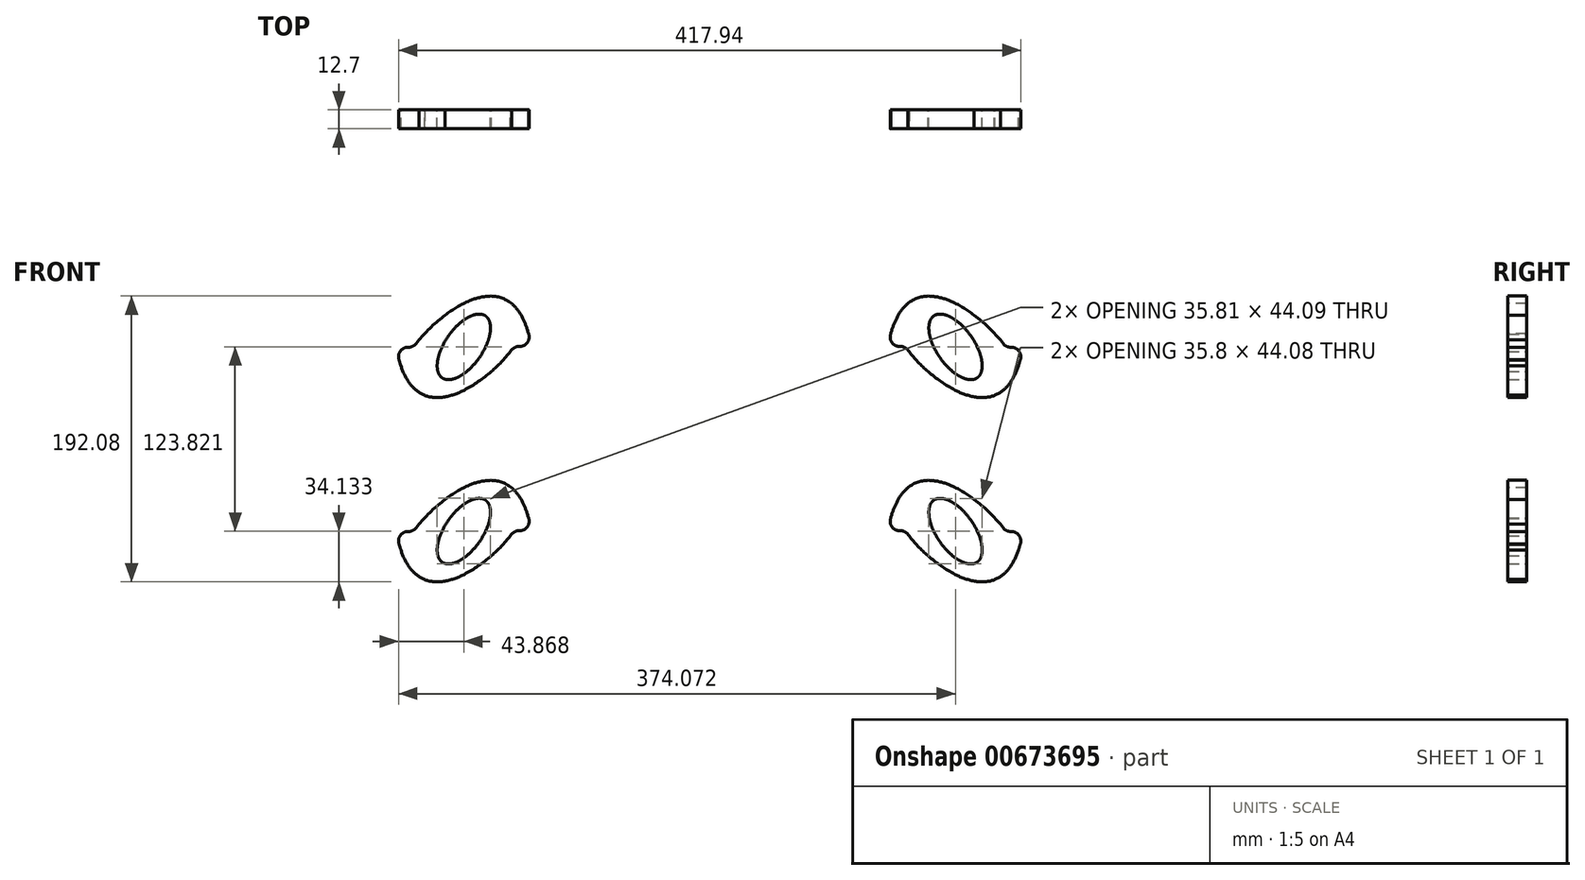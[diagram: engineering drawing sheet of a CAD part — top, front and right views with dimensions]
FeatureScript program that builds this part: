
annotation { "Feature Type Name" : "Feature", "Feature Type Description" : "" }
export const myFeature = defineFeature(function(context is Context, id is Id, definition is map)
    precondition{}
    {
        {
            var Q0;
            Q0=qCreatedBy(makeId("Front.planeOp"),FACE);
            var sketch = newSketch(context, id + "F0", { "sketchPlane" : qUnion([Q0])});
            skArc(sketch, "E0", {"start": v(-195.2, 79.62) * mm, "mid": v(-186.95, 88.48) * mm, "end": v(-177.7, 96.3) * mm});
            skArc(sketch, "E1", {"start": v(-177.7, 96.3) * mm, "mid": v(-169.74, 101.66) * mm, "end": v(-161.19, 106) * mm});
            skArc(sketch, "E2", {"start": v(-161.19, 106) * mm, "mid": v(-154.68, 108.16) * mm, "end": v(-147.88, 109.11) * mm});
            skArc(sketch, "E3", {"start": v(-147.88, 109.11) * mm, "mid": v(-140.03, 108.03) * mm, "end": v(-133.1, 104.19) * mm});
            skArc(sketch, "E4", {"start": v(-133.1, 104.19) * mm, "mid": v(-128.88, 99.71) * mm, "end": v(-125.64, 94.47) * mm});
            skArc(sketch, "E5", {"start": v(-125.64, 94.47) * mm, "mid": v(-123.38, 89.28) * mm, "end": v(-121.63, 83.89) * mm});
            skLineSegment(sketch, "E6", {"start": v(-121.63, 83.89) * mm, "end": v(-121.54, 83.6) * mm});
            skArc(sketch, "E7", {"start": v(-121.54, 83.6) * mm, "mid": v(-122.53, 77.79) * mm, "end": v(-127.86, 75.29) * mm});
            skArc(sketch, "E8", {"start": v(-127.86, 75.29) * mm, "mid": v(-130.86, 74.68) * mm, "end": v(-133.23, 72.74) * mm});
            skLineSegment(sketch, "E9", {"start": v(-133.23, 72.74) * mm, "end": v(-133.9, 71.83) * mm});
            skArc(sketch, "E10", {"start": v(-133.9, 71.83) * mm, "mid": v(-139.92, 64.83) * mm, "end": v(-146.63, 58.5) * mm});
            skArc(sketch, "E11", {"start": v(-146.63, 58.5) * mm, "mid": v(-155.36, 51.67) * mm, "end": v(-164.85, 45.94) * mm});
            skArc(sketch, "E12", {"start": v(-164.85, 45.94) * mm, "mid": v(-171.62, 43.03) * mm, "end": v(-178.77, 41.23) * mm});
            skArc(sketch, "E13", {"start": v(-178.77, 41.23) * mm, "mid": v(-185.1, 40.98) * mm, "end": v(-191.28, 42.4) * mm});
            skLineSegment(sketch, "E14", {"start": v(-191.28, 42.4) * mm, "end": v(-191.47, 42.47) * mm});
            skArc(sketch, "E15", {"start": v(-191.47, 42.47) * mm, "mid": v(-196.89, 45.66) * mm, "end": v(-201.23, 50.2) * mm});
            skArc(sketch, "E16", {"start": v(-201.23, 50.2) * mm, "mid": v(-204.77, 55.97) * mm, "end": v(-207.35, 62.21) * mm});
            skArc(sketch, "E17", {"start": v(-207.35, 62.21) * mm, "mid": v(-207.97, 64.12) * mm, "end": v(-208.54, 66.04) * mm});
            skLineSegment(sketch, "E18", {"start": v(-208.54, 66.04) * mm, "end": v(-208.64, 66.36) * mm});
            skArc(sketch, "E19", {"start": v(-208.64, 66.36) * mm, "mid": v(-207.71, 72.2) * mm, "end": v(-202.4, 74.74) * mm});
            skArc(sketch, "E20", {"start": v(-202.4, 74.74) * mm, "mid": v(-199.51, 75.32) * mm, "end": v(-197.2, 77.12) * mm});
            skLineSegment(sketch, "E21", {"start": v(-197.2, 77.12) * mm, "end": v(-195.2, 79.62) * mm});
            skArc(sketch, "E22", {"start": v(-179.67, 54.2) * mm, "mid": v(-178.37, 53.5) * mm, "end": v(-176.95, 53.1) * mm});
            skArc(sketch, "E23", {"start": v(-176.95, 53.1) * mm, "mid": v(-175.54, 52.97) * mm, "end": v(-174.13, 53.05) * mm});
            skArc(sketch, "E24", {"start": v(-174.13, 53.05) * mm, "mid": v(-172.49, 53.36) * mm, "end": v(-170.89, 53.86) * mm});
            skArc(sketch, "E25", {"start": v(-170.89, 53.86) * mm, "mid": v(-168.9, 54.7) * mm, "end": v(-167, 55.74) * mm});
            skArc(sketch, "E26", {"start": v(-167, 55.74) * mm, "mid": v(-164.64, 57.33) * mm, "end": v(-162.41, 59.1) * mm});
            skArc(sketch, "E27", {"start": v(-162.41, 59.1) * mm, "mid": v(-159.55, 61.82) * mm, "end": v(-156.93, 64.78) * mm});
            skArc(sketch, "E28", {"start": v(-156.93, 64.78) * mm, "mid": v(-155.79, 66.23) * mm, "end": v(-154.7, 67.73) * mm});
            skArc(sketch, "E29", {"start": v(-154.7, 67.73) * mm, "mid": v(-152.2, 71.67) * mm, "end": v(-150.1, 75.83) * mm});
            skArc(sketch, "E30", {"start": v(-150.1, 75.83) * mm, "mid": v(-148.93, 78.75) * mm, "end": v(-148.01, 81.76) * mm});
            skArc(sketch, "E31", {"start": v(-148.01, 81.76) * mm, "mid": v(-147.52, 84.07) * mm, "end": v(-147.24, 86.4) * mm});
            skArc(sketch, "E32", {"start": v(-147.24, 86.4) * mm, "mid": v(-147.2, 88.21) * mm, "end": v(-147.36, 90.02) * mm});
            skArc(sketch, "E33", {"start": v(-147.36, 90.02) * mm, "mid": v(-147.66, 91.45) * mm, "end": v(-148.15, 92.83) * mm});
            skArc(sketch, "E34", {"start": v(-148.15, 92.83) * mm, "mid": v(-148.8, 94.03) * mm, "end": v(-149.67, 95.1) * mm});
            skArc(sketch, "E35", {"start": v(-149.67, 95.1) * mm, "mid": v(-150.08, 95.47) * mm, "end": v(-150.53, 95.82) * mm});
            skArc(sketch, "E36", {"start": v(-150.53, 95.82) * mm, "mid": v(-151.83, 96.52) * mm, "end": v(-153.26, 96.93) * mm});
            skArc(sketch, "E37", {"start": v(-153.26, 96.93) * mm, "mid": v(-154.66, 97.06) * mm, "end": v(-156.07, 96.98) * mm});
            skArc(sketch, "E38", {"start": v(-156.07, 96.98) * mm, "mid": v(-157.72, 96.67) * mm, "end": v(-159.31, 96.17) * mm});
            skArc(sketch, "E39", {"start": v(-159.31, 96.17) * mm, "mid": v(-161.3, 95.32) * mm, "end": v(-163.2, 94.28) * mm});
            skArc(sketch, "E40", {"start": v(-163.2, 94.28) * mm, "mid": v(-165.56, 92.7) * mm, "end": v(-167.8, 90.92) * mm});
            skArc(sketch, "E41", {"start": v(-167.8, 90.92) * mm, "mid": v(-170.66, 88.2) * mm, "end": v(-173.28, 85.25) * mm});
            skArc(sketch, "E42", {"start": v(-173.28, 85.25) * mm, "mid": v(-174.42, 83.8) * mm, "end": v(-175.5, 82.3) * mm});
            skArc(sketch, "E43", {"start": v(-175.5, 82.3) * mm, "mid": v(-178, 78.36) * mm, "end": v(-180.1, 74.2) * mm});
            skArc(sketch, "E44", {"start": v(-180.1, 74.2) * mm, "mid": v(-181.27, 71.27) * mm, "end": v(-182.19, 68.26) * mm});
            skArc(sketch, "E45", {"start": v(-182.19, 68.26) * mm, "mid": v(-182.68, 65.96) * mm, "end": v(-182.96, 63.62) * mm});
            skArc(sketch, "E46", {"start": v(-182.96, 63.62) * mm, "mid": v(-183, 61.81) * mm, "end": v(-182.84, 60) * mm});
            skArc(sketch, "E47", {"start": v(-182.84, 60) * mm, "mid": v(-182.54, 58.58) * mm, "end": v(-182.05, 57.2) * mm});
            skArc(sketch, "E48", {"start": v(-182.05, 57.2) * mm, "mid": v(-181.4, 56) * mm, "end": v(-180.54, 54.94) * mm});
            skArc(sketch, "E49", {"start": v(-180.54, 54.94) * mm, "mid": v(-180.12, 54.55) * mm, "end": v(-179.67, 54.2) * mm});
            skLineSegment(sketch, "E50", {"start": v(195.2, -44.2) * mm, "end": v(197.2, -46.7) * mm});
            skArc(sketch, "E51", {"start": v(197.2, -46.7) * mm, "mid": v(199.51, -48.5) * mm, "end": v(202.4, -49.08) * mm});
            skArc(sketch, "E52", {"start": v(202.4, -49.08) * mm, "mid": v(207.71, -51.63) * mm, "end": v(208.64, -57.46) * mm});
            skLineSegment(sketch, "E53", {"start": v(208.64, -57.46) * mm, "end": v(208.54, -57.78) * mm});
            skArc(sketch, "E54", {"start": v(208.54, -57.78) * mm, "mid": v(207.97, -59.7) * mm, "end": v(207.35, -61.6) * mm});
            skArc(sketch, "E55", {"start": v(207.35, -61.6) * mm, "mid": v(204.77, -67.85) * mm, "end": v(201.23, -73.62) * mm});
            skArc(sketch, "E56", {"start": v(201.23, -73.62) * mm, "mid": v(196.89, -78.16) * mm, "end": v(191.47, -81.35) * mm});
            skLineSegment(sketch, "E57", {"start": v(191.47, -81.35) * mm, "end": v(191.28, -81.43) * mm});
            skArc(sketch, "E58", {"start": v(191.28, -81.43) * mm, "mid": v(185.1, -82.84) * mm, "end": v(178.77, -82.6) * mm});
            skArc(sketch, "E59", {"start": v(178.77, -82.6) * mm, "mid": v(171.62, -80.8) * mm, "end": v(164.85, -77.88) * mm});
            skArc(sketch, "E60", {"start": v(164.85, -77.88) * mm, "mid": v(155.36, -72.15) * mm, "end": v(146.63, -65.33) * mm});
            skArc(sketch, "E61", {"start": v(146.63, -65.33) * mm, "mid": v(139.92, -58.99) * mm, "end": v(133.9, -51.99) * mm});
            skLineSegment(sketch, "E62", {"start": v(133.9, -51.99) * mm, "end": v(133.23, -51.08) * mm});
            skArc(sketch, "E63", {"start": v(133.23, -51.08) * mm, "mid": v(130.86, -49.14) * mm, "end": v(127.86, -48.53) * mm});
            skArc(sketch, "E64", {"start": v(127.86, -48.53) * mm, "mid": v(122.53, -46.04) * mm, "end": v(121.54, -40.23) * mm});
            skLineSegment(sketch, "E65", {"start": v(121.54, -40.23) * mm, "end": v(121.63, -39.93) * mm});
            skArc(sketch, "E66", {"start": v(121.63, -39.93) * mm, "mid": v(123.38, -34.55) * mm, "end": v(125.64, -29.35) * mm});
            skArc(sketch, "E67", {"start": v(125.64, -29.35) * mm, "mid": v(128.88, -24.1) * mm, "end": v(133.1, -19.63) * mm});
            skArc(sketch, "E68", {"start": v(133.1, -19.63) * mm, "mid": v(140.03, -15.79) * mm, "end": v(147.88, -14.7) * mm});
            skArc(sketch, "E69", {"start": v(147.88, -14.7) * mm, "mid": v(154.68, -15.66) * mm, "end": v(161.19, -17.82) * mm});
            skArc(sketch, "E70", {"start": v(161.19, -17.82) * mm, "mid": v(169.74, -22.16) * mm, "end": v(177.7, -27.53) * mm});
            skArc(sketch, "E71", {"start": v(177.7, -27.53) * mm, "mid": v(186.95, -35.34) * mm, "end": v(195.2, -44.2) * mm});
            skArc(sketch, "E72", {"start": v(179.67, -69.61) * mm, "mid": v(180.78, -68.63) * mm, "end": v(181.64, -67.43) * mm});
            skArc(sketch, "E73", {"start": v(181.64, -67.43) * mm, "mid": v(182.25, -66.16) * mm, "end": v(182.65, -64.8) * mm});
            skArc(sketch, "E74", {"start": v(182.65, -64.8) * mm, "mid": v(182.92, -63.15) * mm, "end": v(183, -61.48) * mm});
            skArc(sketch, "E75", {"start": v(183, -61.48) * mm, "mid": v(182.88, -59.32) * mm, "end": v(182.56, -57.19) * mm});
            skArc(sketch, "E76", {"start": v(182.56, -57.19) * mm, "mid": v(181.88, -54.42) * mm, "end": v(180.97, -51.72) * mm});
            skArc(sketch, "E77", {"start": v(180.97, -51.72) * mm, "mid": v(179.4, -48.1) * mm, "end": v(177.51, -44.63) * mm});
            skArc(sketch, "E78", {"start": v(177.51, -44.63) * mm, "mid": v(176.54, -43.06) * mm, "end": v(175.5, -41.52) * mm});
            skArc(sketch, "E79", {"start": v(175.5, -41.52) * mm, "mid": v(172.66, -37.83) * mm, "end": v(169.47, -34.43) * mm});
            skArc(sketch, "E80", {"start": v(169.47, -34.43) * mm, "mid": v(167.12, -32.33) * mm, "end": v(164.6, -30.44) * mm});
            skArc(sketch, "E81", {"start": v(164.6, -30.44) * mm, "mid": v(162.6, -29.2) * mm, "end": v(160.5, -28.13) * mm});
            skArc(sketch, "E82", {"start": v(160.5, -28.13) * mm, "mid": v(158.82, -27.48) * mm, "end": v(157.07, -27) * mm});
            skArc(sketch, "E83", {"start": v(157.07, -27) * mm, "mid": v(155.62, -26.8) * mm, "end": v(154.16, -26.78) * mm});
            skArc(sketch, "E84", {"start": v(154.16, -26.78) * mm, "mid": v(152.8, -26.99) * mm, "end": v(151.51, -27.44) * mm});
            skArc(sketch, "E85", {"start": v(151.51, -27.44) * mm, "mid": v(151.01, -27.7) * mm, "end": v(150.53, -28) * mm});
            skArc(sketch, "E86", {"start": v(150.53, -28) * mm, "mid": v(149.43, -28.98) * mm, "end": v(148.56, -30.18) * mm});
            skArc(sketch, "E87", {"start": v(148.56, -30.18) * mm, "mid": v(147.96, -31.46) * mm, "end": v(147.55, -32.8) * mm});
            skArc(sketch, "E88", {"start": v(147.55, -32.8) * mm, "mid": v(147.28, -34.46) * mm, "end": v(147.2, -36.13) * mm});
            skArc(sketch, "E89", {"start": v(147.2, -36.13) * mm, "mid": v(147.32, -38.3) * mm, "end": v(147.65, -40.43) * mm});
            skArc(sketch, "E90", {"start": v(147.65, -40.43) * mm, "mid": v(148.32, -43.2) * mm, "end": v(149.23, -45.9) * mm});
            skArc(sketch, "E91", {"start": v(149.23, -45.9) * mm, "mid": v(150.8, -49.52) * mm, "end": v(152.7, -52.99) * mm});
            skArc(sketch, "E92", {"start": v(152.7, -52.99) * mm, "mid": v(153.67, -54.56) * mm, "end": v(154.7, -56.1) * mm});
            skArc(sketch, "E93", {"start": v(154.7, -56.1) * mm, "mid": v(157.55, -59.78) * mm, "end": v(160.74, -63.19) * mm});
            skArc(sketch, "E94", {"start": v(160.74, -63.19) * mm, "mid": v(163.09, -65.28) * mm, "end": v(165.6, -67.17) * mm});
            skArc(sketch, "E95", {"start": v(165.6, -67.17) * mm, "mid": v(167.6, -68.42) * mm, "end": v(169.7, -69.48) * mm});
            skArc(sketch, "E96", {"start": v(169.7, -69.48) * mm, "mid": v(171.39, -70.14) * mm, "end": v(173.13, -70.6) * mm});
            skArc(sketch, "E97", {"start": v(173.13, -70.6) * mm, "mid": v(174.58, -70.82) * mm, "end": v(176.05, -70.83) * mm});
            skArc(sketch, "E98", {"start": v(176.05, -70.83) * mm, "mid": v(177.4, -70.63) * mm, "end": v(178.69, -70.18) * mm});
            skArc(sketch, "E99", {"start": v(178.69, -70.18) * mm, "mid": v(179.2, -69.92) * mm, "end": v(179.67, -69.61) * mm});
            skLineSegment(sketch, "E100", {"start": v(195.2, 79.62) * mm, "end": v(197.2, 77.12) * mm});
            skArc(sketch, "E101", {"start": v(197.2, 77.12) * mm, "mid": v(199.51, 75.32) * mm, "end": v(202.4, 74.74) * mm});
            skArc(sketch, "E102", {"start": v(202.4, 74.74) * mm, "mid": v(207.71, 72.2) * mm, "end": v(208.64, 66.36) * mm});
            skLineSegment(sketch, "E103", {"start": v(208.64, 66.36) * mm, "end": v(208.54, 66.04) * mm});
            skArc(sketch, "E104", {"start": v(208.54, 66.04) * mm, "mid": v(207.97, 64.12) * mm, "end": v(207.35, 62.21) * mm});
            skArc(sketch, "E105", {"start": v(207.35, 62.21) * mm, "mid": v(204.77, 55.97) * mm, "end": v(201.23, 50.2) * mm});
            skArc(sketch, "E106", {"start": v(201.23, 50.2) * mm, "mid": v(196.89, 45.66) * mm, "end": v(191.47, 42.47) * mm});
            skLineSegment(sketch, "E107", {"start": v(191.47, 42.47) * mm, "end": v(191.28, 42.4) * mm});
            skArc(sketch, "E108", {"start": v(191.28, 42.4) * mm, "mid": v(185.1, 40.98) * mm, "end": v(178.77, 41.23) * mm});
            skArc(sketch, "E109", {"start": v(178.77, 41.23) * mm, "mid": v(171.62, 43.03) * mm, "end": v(164.85, 45.94) * mm});
            skArc(sketch, "E110", {"start": v(164.85, 45.94) * mm, "mid": v(155.36, 51.67) * mm, "end": v(146.63, 58.5) * mm});
            skArc(sketch, "E111", {"start": v(146.63, 58.5) * mm, "mid": v(139.92, 64.83) * mm, "end": v(133.9, 71.83) * mm});
            skLineSegment(sketch, "E112", {"start": v(133.9, 71.83) * mm, "end": v(133.23, 72.74) * mm});
            skArc(sketch, "E113", {"start": v(133.23, 72.74) * mm, "mid": v(130.86, 74.68) * mm, "end": v(127.86, 75.29) * mm});
            skArc(sketch, "E114", {"start": v(127.86, 75.29) * mm, "mid": v(122.53, 77.79) * mm, "end": v(121.54, 83.6) * mm});
            skLineSegment(sketch, "E115", {"start": v(121.54, 83.6) * mm, "end": v(121.63, 83.89) * mm});
            skArc(sketch, "E116", {"start": v(121.63, 83.89) * mm, "mid": v(123.38, 89.28) * mm, "end": v(125.64, 94.47) * mm});
            skArc(sketch, "E117", {"start": v(125.64, 94.47) * mm, "mid": v(128.88, 99.71) * mm, "end": v(133.1, 104.19) * mm});
            skArc(sketch, "E118", {"start": v(133.1, 104.19) * mm, "mid": v(140.03, 108.03) * mm, "end": v(147.88, 109.11) * mm});
            skArc(sketch, "E119", {"start": v(147.88, 109.11) * mm, "mid": v(154.68, 108.16) * mm, "end": v(161.19, 106) * mm});
            skArc(sketch, "E120", {"start": v(161.19, 106) * mm, "mid": v(169.74, 101.66) * mm, "end": v(177.7, 96.3) * mm});
            skArc(sketch, "E121", {"start": v(177.7, 96.3) * mm, "mid": v(186.95, 88.48) * mm, "end": v(195.2, 79.62) * mm});
            skArc(sketch, "E122", {"start": v(179.67, 54.2) * mm, "mid": v(180.78, 55.19) * mm, "end": v(181.64, 56.39) * mm});
            skArc(sketch, "E123", {"start": v(181.64, 56.39) * mm, "mid": v(182.25, 57.66) * mm, "end": v(182.65, 59.01) * mm});
            skArc(sketch, "E124", {"start": v(182.65, 59.01) * mm, "mid": v(182.92, 60.67) * mm, "end": v(183, 62.34) * mm});
            skArc(sketch, "E125", {"start": v(183, 62.34) * mm, "mid": v(182.88, 64.5) * mm, "end": v(182.56, 66.63) * mm});
            skArc(sketch, "E126", {"start": v(182.56, 66.63) * mm, "mid": v(181.88, 69.4) * mm, "end": v(180.97, 72.1) * mm});
            skArc(sketch, "E127", {"start": v(180.97, 72.1) * mm, "mid": v(179.4, 75.72) * mm, "end": v(177.51, 79.2) * mm});
            skArc(sketch, "E128", {"start": v(177.51, 79.2) * mm, "mid": v(176.54, 80.76) * mm, "end": v(175.5, 82.3) * mm});
            skArc(sketch, "E129", {"start": v(175.5, 82.3) * mm, "mid": v(172.66, 86) * mm, "end": v(169.47, 89.4) * mm});
            skArc(sketch, "E130", {"start": v(169.47, 89.4) * mm, "mid": v(167.12, 91.49) * mm, "end": v(164.6, 93.38) * mm});
            skArc(sketch, "E131", {"start": v(164.6, 93.38) * mm, "mid": v(162.6, 94.63) * mm, "end": v(160.5, 95.69) * mm});
            skArc(sketch, "E132", {"start": v(160.5, 95.69) * mm, "mid": v(158.82, 96.34) * mm, "end": v(157.07, 96.82) * mm});
            skArc(sketch, "E133", {"start": v(157.07, 96.82) * mm, "mid": v(155.62, 97.02) * mm, "end": v(154.16, 97.04) * mm});
            skArc(sketch, "E134", {"start": v(154.16, 97.04) * mm, "mid": v(152.8, 96.83) * mm, "end": v(151.51, 96.39) * mm});
            skArc(sketch, "E135", {"start": v(151.51, 96.39) * mm, "mid": v(151.01, 96.12) * mm, "end": v(150.53, 95.82) * mm});
            skArc(sketch, "E136", {"start": v(150.53, 95.82) * mm, "mid": v(149.43, 94.84) * mm, "end": v(148.56, 93.64) * mm});
            skArc(sketch, "E137", {"start": v(148.56, 93.64) * mm, "mid": v(147.96, 92.36) * mm, "end": v(147.55, 91.01) * mm});
            skArc(sketch, "E138", {"start": v(147.55, 91.01) * mm, "mid": v(147.28, 89.36) * mm, "end": v(147.2, 87.69) * mm});
            skArc(sketch, "E139", {"start": v(147.2, 87.69) * mm, "mid": v(147.32, 85.53) * mm, "end": v(147.65, 83.4) * mm});
            skArc(sketch, "E140", {"start": v(147.65, 83.4) * mm, "mid": v(148.32, 80.63) * mm, "end": v(149.23, 77.93) * mm});
            skArc(sketch, "E141", {"start": v(149.23, 77.93) * mm, "mid": v(150.8, 74.3) * mm, "end": v(152.7, 70.83) * mm});
            skArc(sketch, "E142", {"start": v(152.7, 70.83) * mm, "mid": v(153.67, 69.26) * mm, "end": v(154.7, 67.73) * mm});
            skArc(sketch, "E143", {"start": v(154.7, 67.73) * mm, "mid": v(157.55, 64.04) * mm, "end": v(160.74, 60.63) * mm});
            skArc(sketch, "E144", {"start": v(160.74, 60.63) * mm, "mid": v(163.09, 58.54) * mm, "end": v(165.6, 56.65) * mm});
            skArc(sketch, "E145", {"start": v(165.6, 56.65) * mm, "mid": v(167.6, 55.4) * mm, "end": v(169.7, 54.34) * mm});
            skArc(sketch, "E146", {"start": v(169.7, 54.34) * mm, "mid": v(171.39, 53.68) * mm, "end": v(173.13, 53.21) * mm});
            skArc(sketch, "E147", {"start": v(173.13, 53.21) * mm, "mid": v(174.58, 53) * mm, "end": v(176.05, 53) * mm});
            skArc(sketch, "E148", {"start": v(176.05, 53) * mm, "mid": v(177.4, 53.2) * mm, "end": v(178.69, 53.64) * mm});
            skArc(sketch, "E149", {"start": v(178.69, 53.64) * mm, "mid": v(179.2, 53.9) * mm, "end": v(179.67, 54.2) * mm});
            skArc(sketch, "E150", {"start": v(-195.2, -44.2) * mm, "mid": v(-186.95, -35.34) * mm, "end": v(-177.7, -27.53) * mm});
            skArc(sketch, "E151", {"start": v(-177.7, -27.53) * mm, "mid": v(-169.74, -22.16) * mm, "end": v(-161.19, -17.82) * mm});
            skArc(sketch, "E152", {"start": v(-161.19, -17.82) * mm, "mid": v(-154.68, -15.66) * mm, "end": v(-147.88, -14.7) * mm});
            skArc(sketch, "E153", {"start": v(-147.88, -14.7) * mm, "mid": v(-140.03, -15.79) * mm, "end": v(-133.1, -19.63) * mm});
            skArc(sketch, "E154", {"start": v(-133.1, -19.63) * mm, "mid": v(-128.88, -24.1) * mm, "end": v(-125.64, -29.35) * mm});
            skArc(sketch, "E155", {"start": v(-125.64, -29.35) * mm, "mid": v(-123.38, -34.55) * mm, "end": v(-121.63, -39.93) * mm});
            skLineSegment(sketch, "E156", {"start": v(-121.63, -39.93) * mm, "end": v(-121.54, -40.23) * mm});
            skArc(sketch, "E157", {"start": v(-121.54, -40.23) * mm, "mid": v(-122.53, -46.04) * mm, "end": v(-127.86, -48.53) * mm});
            skArc(sketch, "E158", {"start": v(-127.86, -48.53) * mm, "mid": v(-130.86, -49.14) * mm, "end": v(-133.23, -51.08) * mm});
            skLineSegment(sketch, "E159", {"start": v(-133.23, -51.08) * mm, "end": v(-133.9, -51.99) * mm});
            skArc(sketch, "E160", {"start": v(-133.9, -51.99) * mm, "mid": v(-139.92, -58.99) * mm, "end": v(-146.63, -65.33) * mm});
            skArc(sketch, "E161", {"start": v(-146.63, -65.33) * mm, "mid": v(-155.36, -72.15) * mm, "end": v(-164.85, -77.88) * mm});
            skArc(sketch, "E162", {"start": v(-164.85, -77.88) * mm, "mid": v(-171.62, -80.8) * mm, "end": v(-178.77, -82.6) * mm});
            skArc(sketch, "E163", {"start": v(-178.77, -82.6) * mm, "mid": v(-185.1, -82.84) * mm, "end": v(-191.28, -81.43) * mm});
            skLineSegment(sketch, "E164", {"start": v(-191.28, -81.43) * mm, "end": v(-191.47, -81.35) * mm});
            skArc(sketch, "E165", {"start": v(-191.47, -81.35) * mm, "mid": v(-196.89, -78.16) * mm, "end": v(-201.23, -73.62) * mm});
            skArc(sketch, "E166", {"start": v(-201.23, -73.62) * mm, "mid": v(-204.77, -67.85) * mm, "end": v(-207.35, -61.6) * mm});
            skArc(sketch, "E167", {"start": v(-207.35, -61.6) * mm, "mid": v(-207.97, -59.7) * mm, "end": v(-208.54, -57.78) * mm});
            skLineSegment(sketch, "E168", {"start": v(-208.54, -57.78) * mm, "end": v(-208.64, -57.46) * mm});
            skArc(sketch, "E169", {"start": v(-208.64, -57.46) * mm, "mid": v(-207.71, -51.63) * mm, "end": v(-202.4, -49.08) * mm});
            skArc(sketch, "E170", {"start": v(-202.4, -49.08) * mm, "mid": v(-199.51, -48.5) * mm, "end": v(-197.2, -46.7) * mm});
            skLineSegment(sketch, "E171", {"start": v(-197.2, -46.7) * mm, "end": v(-195.2, -44.2) * mm});
            skArc(sketch, "E172", {"start": v(-179.67, -69.61) * mm, "mid": v(-178.37, -70.32) * mm, "end": v(-176.95, -70.72) * mm});
            skArc(sketch, "E173", {"start": v(-176.95, -70.72) * mm, "mid": v(-175.54, -70.85) * mm, "end": v(-174.13, -70.77) * mm});
            skArc(sketch, "E174", {"start": v(-174.13, -70.77) * mm, "mid": v(-172.49, -70.46) * mm, "end": v(-170.89, -69.96) * mm});
            skArc(sketch, "E175", {"start": v(-170.89, -69.96) * mm, "mid": v(-168.9, -69.11) * mm, "end": v(-167, -68.08) * mm});
            skArc(sketch, "E176", {"start": v(-167, -68.08) * mm, "mid": v(-164.64, -66.5) * mm, "end": v(-162.41, -64.71) * mm});
            skArc(sketch, "E177", {"start": v(-162.41, -64.71) * mm, "mid": v(-159.55, -62) * mm, "end": v(-156.93, -59.04) * mm});
            skArc(sketch, "E178", {"start": v(-156.93, -59.04) * mm, "mid": v(-155.79, -57.59) * mm, "end": v(-154.7, -56.1) * mm});
            skArc(sketch, "E179", {"start": v(-154.7, -56.1) * mm, "mid": v(-152.2, -52.15) * mm, "end": v(-150.1, -48) * mm});
            skArc(sketch, "E180", {"start": v(-150.1, -48) * mm, "mid": v(-148.93, -45.07) * mm, "end": v(-148.01, -42.06) * mm});
            skArc(sketch, "E181", {"start": v(-148.01, -42.06) * mm, "mid": v(-147.52, -39.75) * mm, "end": v(-147.24, -37.42) * mm});
            skArc(sketch, "E182", {"start": v(-147.24, -37.42) * mm, "mid": v(-147.2, -35.6) * mm, "end": v(-147.36, -33.8) * mm});
            skArc(sketch, "E183", {"start": v(-147.36, -33.8) * mm, "mid": v(-147.66, -32.37) * mm, "end": v(-148.15, -31) * mm});
            skArc(sketch, "E184", {"start": v(-148.15, -31) * mm, "mid": v(-148.8, -29.8) * mm, "end": v(-149.67, -28.73) * mm});
            skArc(sketch, "E185", {"start": v(-149.67, -28.73) * mm, "mid": v(-150.08, -28.35) * mm, "end": v(-150.53, -28) * mm});
            skArc(sketch, "E186", {"start": v(-150.53, -28) * mm, "mid": v(-151.83, -27.3) * mm, "end": v(-153.26, -26.9) * mm});
            skArc(sketch, "E187", {"start": v(-153.26, -26.9) * mm, "mid": v(-154.66, -26.76) * mm, "end": v(-156.07, -26.84) * mm});
            skArc(sketch, "E188", {"start": v(-156.07, -26.84) * mm, "mid": v(-157.72, -27.15) * mm, "end": v(-159.31, -27.65) * mm});
            skArc(sketch, "E189", {"start": v(-159.31, -27.65) * mm, "mid": v(-161.3, -28.5) * mm, "end": v(-163.2, -29.54) * mm});
            skArc(sketch, "E190", {"start": v(-163.2, -29.54) * mm, "mid": v(-165.56, -31.12) * mm, "end": v(-167.8, -32.9) * mm});
            skArc(sketch, "E191", {"start": v(-167.8, -32.9) * mm, "mid": v(-170.66, -35.62) * mm, "end": v(-173.28, -38.58) * mm});
            skArc(sketch, "E192", {"start": v(-173.28, -38.57) * mm, "mid": v(-174.42, -40.03) * mm, "end": v(-175.5, -41.52) * mm});
            skArc(sketch, "E193", {"start": v(-175.5, -41.52) * mm, "mid": v(-178, -45.46) * mm, "end": v(-180.1, -49.62) * mm});
            skArc(sketch, "E194", {"start": v(-180.1, -49.62) * mm, "mid": v(-181.27, -52.55) * mm, "end": v(-182.19, -55.56) * mm});
            skArc(sketch, "E195", {"start": v(-182.19, -55.56) * mm, "mid": v(-182.68, -57.86) * mm, "end": v(-182.96, -60.2) * mm});
            skArc(sketch, "E196", {"start": v(-182.96, -60.2) * mm, "mid": v(-183, -62) * mm, "end": v(-182.84, -63.81) * mm});
            skArc(sketch, "E197", {"start": v(-182.84, -63.81) * mm, "mid": v(-182.54, -65.25) * mm, "end": v(-182.05, -66.62) * mm});
            skArc(sketch, "E198", {"start": v(-182.05, -66.62) * mm, "mid": v(-181.4, -67.82) * mm, "end": v(-180.54, -68.88) * mm});
            skArc(sketch, "E199", {"start": v(-180.54, -68.88) * mm, "mid": v(-180.12, -69.27) * mm, "end": v(-179.67, -69.61) * mm});
            skSolve(sketch);
        }
        {
            var Q0;
            Q0 = qSketchRegion(id + "F0", true);
            extrude(context, id + "F1", {"entities" : qUnion([Q0]), "depth" : 12.7 * mm, "offsetDistance" : 25.4 * mm});
        }
    });
